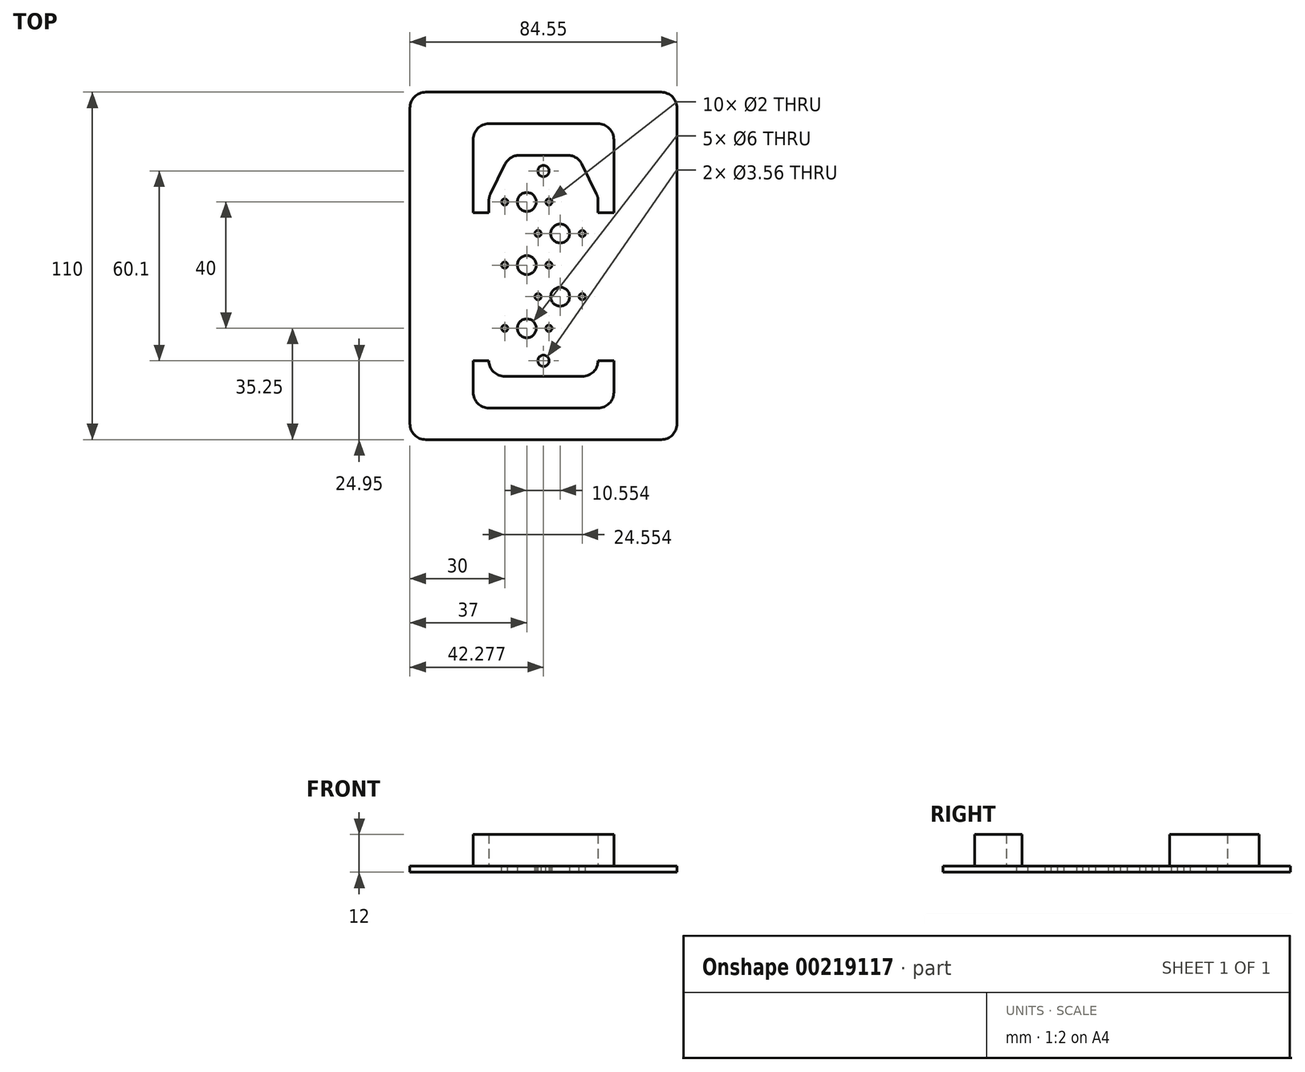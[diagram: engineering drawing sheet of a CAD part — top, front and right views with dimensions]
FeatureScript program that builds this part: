
annotation { "Feature Type Name" : "Feature", "Feature Type Description" : "" }
export const myFeature = defineFeature(function(context is Context, id is Id, definition is map)
    precondition{}
    {
        {
            var Q0;
            Q0=qCreatedBy(makeId("Top.planeOp"),FACE);
            var sketch = newSketch(context, id + "F0", { "sketchPlane" : qUnion([Q0])});
            skLineSegment(sketch, "E0", {"start": v(0, 0) * mm, "end": v(0, 5) * mm});
            skLineSegment(sketch, "E1", {"start": v(0, 56.78) * mm, "end": v(6.48, 70) * mm});
            skLineSegment(sketch, "E2", {"start": v(6.48, 70) * mm, "end": v(28.07, 70) * mm});
            skLineSegment(sketch, "E3", {"start": v(28.07, 70) * mm, "end": v(34.55, 56.78) * mm});
            skLineSegment(sketch, "E4", {"start": v(34.55, 56.78) * mm, "end": v(34.55, 51.78) * mm});
            skLineSegment(sketch, "E5", {"start": v(34.55, 0) * mm, "end": v(0, 0) * mm});
            skLineSegment(sketch, "E6", {"start": v(0, 51.78) * mm, "end": v(-5, 51.78) * mm});
            skLineSegment(sketch, "E7", {"start": v(-5, 51.78) * mm, "end": v(-5, 80) * mm});
            skLineSegment(sketch, "E8", {"start": v(-5, 80) * mm, "end": v(39.55, 80) * mm});
            skLineSegment(sketch, "E9", {"start": v(39.55, 80) * mm, "end": v(39.55, 51.78) * mm});
            skLineSegment(sketch, "E10", {"start": v(39.55, 51.78) * mm, "end": v(34.55, 51.78) * mm});
            skLineSegment(sketch, "E11", {"start": v(0, 5) * mm, "end": v(-5, 5) * mm});
            skLineSegment(sketch, "E12", {"start": v(-5, 5) * mm, "end": v(-5, -10) * mm});
            skLineSegment(sketch, "E13", {"start": v(-5, -10) * mm, "end": v(39.55, -10) * mm});
            skLineSegment(sketch, "E14", {"start": v(39.55, -10) * mm, "end": v(39.55, 5) * mm});
            skLineSegment(sketch, "E15", {"start": v(39.55, 5) * mm, "end": v(34.55, 5) * mm});
            skLineSegment(sketch, "E16", {"start": v(17.28, 70) * mm, "end": v(17.28, 0) * mm, "construction": true});
            skCircle(sketch, "E17", {"center": v(17.28, 65.05) * mm, "radius": 1.78 * mm});
            skCircle(sketch, "E18", {"center": v(17.28, 4.95) * mm, "radius": 1.78 * mm});
            skCircle(sketch, "E19", {"center": v(12, 35.25) * mm, "radius": 3 * mm});
            skCircle(sketch, "E20", {"center": v(22.55, 45.25) * mm, "radius": 3 * mm});
            skCircle(sketch, "E21", {"center": v(22.55, 25.25) * mm, "radius": 3 * mm});
            skCircle(sketch, "E22", {"center": v(12, 15.25) * mm, "radius": 3 * mm});
            skCircle(sketch, "E23", {"center": v(12, 55.25) * mm, "radius": 3 * mm});
            skPoint(sketch, "E24.startSnap0", {"position": v(17.28, 80) * mm});
            skPoint(sketch, "E25.endSnap0", {"position": v(0, 28.39) * mm});
            skLineSegment(sketch, "E26.bottom", {"start": v(-25, 90) * mm, "end": v(59.55, 90) * mm});
            skLineSegment(sketch, "E26.top", {"start": v(-25, -20) * mm, "end": v(59.55, -20) * mm});
            skLineSegment(sketch, "E26.left", {"start": v(-25, 90) * mm, "end": v(-25, -20) * mm});
            skLineSegment(sketch, "E26.right", {"start": v(59.55, 90) * mm, "end": v(59.55, -20) * mm});
            skLineSegment(sketch, "E27.trimOffspring", {"start": v(0, 51.78) * mm, "end": v(0, 56.78) * mm});
            skLineSegment(sketch, "E28.trimOffspring", {"start": v(34.55, 5) * mm, "end": v(34.55, 0) * mm});
            skSolve(sketch);
        }
        {
            var Q0;
            Q0=makeQuery(id+"F0.imprint","IMPRINT",FACE,{"disambiguationData":[TD([[makeQuery(id+"F0.imprint","IMPRINT",EDGE,{"derivedFrom":sQuery(id+"F0.wireOp",EDGE,"E0")}),-1.0]])]});
            extrude(context, id + "F1", {"entities" : qUnion([Q0]), "depth" : 2 * mm});
        }
        {
            var Q0;
            Q0=makeQuery(id+"F0.imprint","IMPRINT",FACE,{"disambiguationData":[TD([[makeQuery(id+"F0.imprint","IMPRINT",EDGE,{"derivedFrom":sQuery(id+"F0.wireOp",EDGE,"E1")}),1.0]])]});
            extrude(context, id + "F2", {"entities" : qUnion([Q0]), "operationType" : NewBodyOperationType.ADD, "depth" : 12 * mm});
        }
        {
            var Q0;
            Q0=makeQuery(id+"F0.imprint","IMPRINT",FACE,{"disambiguationData":[TD([[makeQuery(id+"F0.imprint","IMPRINT",EDGE,{"derivedFrom":sQuery(id+"F0.wireOp",EDGE,"E0")}),1.0]])]});
            extrude(context, id + "F3", {"entities" : qUnion([Q0]), "operationType" : NewBodyOperationType.ADD, "depth" : 12 * mm});
        }
        {
            var Q0;
            Q0=makeQuery(id+"F2.opExtrude","SWEPT_EDGE",EDGE,{"disambiguationData":[OSD([sQuery(id+"F0.wireOp",EDGE,"E1"),sQuery(id+"F0.wireOp",EDGE,"E2")])]});
            var Q1;
            Q1=makeQuery(id+"F2.opExtrude","SWEPT_EDGE",EDGE,{"disambiguationData":[OSD([sQuery(id+"F0.wireOp",EDGE,"E2"),sQuery(id+"F0.wireOp",EDGE,"E3")])]});
            var Q2;
            Q2=makeQuery(id+"F2.opExtrude","SWEPT_EDGE",EDGE,{"disambiguationData":[OSD([sQuery(id+"F0.wireOp",EDGE,"E1"),sQuery(id+"F0.wireOp",EDGE,"E27.trimOffspring")])]});
            var Q3;
            Q3=makeQuery(id+"F2.opExtrude","SWEPT_EDGE",EDGE,{"disambiguationData":[OSD([sQuery(id+"F0.wireOp",EDGE,"E3"),sQuery(id+"F0.wireOp",EDGE,"E4")])]});
            var Q4;
            Q4=makeQuery(id+"F3.opExtrude","SWEPT_EDGE",EDGE,{"disambiguationData":[OSD([sQuery(id+"F0.wireOp",EDGE,"E5"),sQuery(id+"F0.wireOp",EDGE,"E28.trimOffspring")])]});
            var Q5;
            Q5=makeQuery(id+"F3.opExtrude","SWEPT_EDGE",EDGE,{"disambiguationData":[OSD([sQuery(id+"F0.wireOp",EDGE,"E0"),sQuery(id+"F0.wireOp",EDGE,"E5")])]});
            var Q6;
            Q6=makeQuery(id+"F1.opExtrude","SWEPT_EDGE",EDGE,{"disambiguationData":[OSD([sQuery(id+"F0.wireOp",EDGE,"E26.top"),sQuery(id+"F0.wireOp",EDGE,"E26.right")])]});
            var Q7;
            Q7=makeQuery(id+"F1.opExtrude","SWEPT_EDGE",EDGE,{"disambiguationData":[OSD([sQuery(id+"F0.wireOp",EDGE,"E26.bottom"),sQuery(id+"F0.wireOp",EDGE,"E26.right")])]});
            var Q8;
            Q8=makeQuery(id+"F1.opExtrude","SWEPT_EDGE",EDGE,{"disambiguationData":[OSD([sQuery(id+"F0.wireOp",EDGE,"E26.bottom"),sQuery(id+"F0.wireOp",EDGE,"E26.left")])]});
            var Q9;
            Q9=makeQuery(id+"F1.opExtrude","SWEPT_EDGE",EDGE,{"disambiguationData":[OSD([sQuery(id+"F0.wireOp",EDGE,"E26.top"),sQuery(id+"F0.wireOp",EDGE,"E26.left")])]});
            fillet(context, id + "F4", {"entities" : qUnion([Q0, Q1, Q2, Q3, Q4, Q5, Q6, Q7, Q8, Q9]), "radius" : 5 * mm, "tangentPropagation" : true, "allowEdgeOverflow" : false});
        }
        {
            var Q0;
            Q0=makeQuery(id+"F3.opExtrude","SWEPT_EDGE",EDGE,{"disambiguationData":[OSD([sQuery(id+"F0.wireOp",EDGE,"E12"),sQuery(id+"F0.wireOp",EDGE,"E13")])]});
            var Q1;
            Q1=makeQuery(id+"F3.opExtrude","SWEPT_EDGE",EDGE,{"disambiguationData":[OSD([sQuery(id+"F0.wireOp",EDGE,"E13"),sQuery(id+"F0.wireOp",EDGE,"E14")])]});
            var Q2;
            Q2=makeQuery(id+"F2.opExtrude","SWEPT_EDGE",EDGE,{"disambiguationData":[OSD([sQuery(id+"F0.wireOp",EDGE,"E8"),sQuery(id+"F0.wireOp",EDGE,"E9")])]});
            var Q3;
            Q3=makeQuery(id+"F2.opExtrude","SWEPT_EDGE",EDGE,{"disambiguationData":[OSD([sQuery(id+"F0.wireOp",EDGE,"E7"),sQuery(id+"F0.wireOp",EDGE,"E8")])]});
            fillet(context, id + "F5", {"entities" : qUnion([Q0, Q1, Q2, Q3]), "radius" : 5 * mm, "tangentPropagation" : true, "allowEdgeOverflow" : false});
        }
        {
            var Q0;
            Q0=makeQuery(id+"F1.opExtrude","CAP_FACE",FACE,{"disambiguationData":[OSD([sQuery(id+"F0.wireOp",EDGE,"E0"),sQuery(id+"F0.wireOp",EDGE,"E1"),sQuery(id+"F0.wireOp",EDGE,"E2"),sQuery(id+"F0.wireOp",EDGE,"E3"),sQuery(id+"F0.wireOp",EDGE,"E4"),sQuery(id+"F0.wireOp",EDGE,"E5"),sQuery(id+"F0.wireOp",EDGE,"E6"),sQuery(id+"F0.wireOp",EDGE,"E7"),sQuery(id+"F0.wireOp",EDGE,"E8"),sQuery(id+"F0.wireOp",EDGE,"E9"),sQuery(id+"F0.wireOp",EDGE,"E10"),sQuery(id+"F0.wireOp",EDGE,"E11"),sQuery(id+"F0.wireOp",EDGE,"E12"),sQuery(id+"F0.wireOp",EDGE,"E13"),sQuery(id+"F0.wireOp",EDGE,"E14"),sQuery(id+"F0.wireOp",EDGE,"E15"),sQuery(id+"F0.wireOp",EDGE,"E17"),sQuery(id+"F0.wireOp",EDGE,"E18"),sQuery(id+"F0.wireOp",EDGE,"E19"),sQuery(id+"F0.wireOp",EDGE,"E20"),sQuery(id+"F0.wireOp",EDGE,"E21"),sQuery(id+"F0.wireOp",EDGE,"E22"),sQuery(id+"F0.wireOp",EDGE,"E23"),sQuery(id+"F0.wireOp",EDGE,"E26.bottom"),sQuery(id+"F0.wireOp",EDGE,"E26.top"),sQuery(id+"F0.wireOp",EDGE,"E26.left"),sQuery(id+"F0.wireOp",EDGE,"E26.right"),sQuery(id+"F0.wireOp",EDGE,"E27.trimOffspring"),sQuery(id+"F0.wireOp",EDGE,"E28.trimOffspring")])],"isStart":false});
            var sketch = newSketch(context, id + "F6", { "sketchPlane" : qUnion([Q0])});
            skCircle(sketch, "E29", {"center": v(5, 55.25) * mm, "radius": 1 * mm});
            skCircle(sketch, "E30", {"center": v(19, 55.25) * mm, "radius": 1 * mm});
            skCircle(sketch, "E31", {"center": v(19, 35.25) * mm, "radius": 1 * mm});
            skCircle(sketch, "E32", {"center": v(5, 35.25) * mm, "radius": 1 * mm});
            skCircle(sketch, "E33", {"center": v(15.55, 25.25) * mm, "radius": 1 * mm});
            skCircle(sketch, "E34", {"center": v(29.55, 25.25) * mm, "radius": 1 * mm});
            skCircle(sketch, "E35", {"center": v(15.55, 45.25) * mm, "radius": 1 * mm});
            skCircle(sketch, "E36", {"center": v(29.55, 45.25) * mm, "radius": 1 * mm});
            skCircle(sketch, "E37", {"center": v(5, 15.25) * mm, "radius": 1 * mm});
            skCircle(sketch, "E38", {"center": v(19, 15.25) * mm, "radius": 1 * mm});
            skSolve(sketch);
        }
        {
            var Q0;
            Q0=makeQuery(id+"F6.imprint","IMPRINT",FACE,{"disambiguationData":[TD([[makeQuery(id+"F6.imprint","IMPRINT",EDGE,{"derivedFrom":sQuery(id+"F6.wireOp",EDGE,"E29")}),1.0]])]});
            var Q1;
            Q1=makeQuery(id+"F6.imprint","IMPRINT",FACE,{"disambiguationData":[TD([[makeQuery(id+"F6.imprint","IMPRINT",EDGE,{"derivedFrom":sQuery(id+"F6.wireOp",EDGE,"E30")}),1.0]])]});
            var Q2;
            Q2=makeQuery(id+"F6.imprint","IMPRINT",FACE,{"disambiguationData":[TD([[makeQuery(id+"F6.imprint","IMPRINT",EDGE,{"derivedFrom":sQuery(id+"F6.wireOp",EDGE,"OHU8HePS-A5hE-2PZY-Okrr-ufKmC9e9iSHk")}),1.0]])]});
            var Q3;
            Q3=makeQuery(id+"F6.imprint","IMPRINT",FACE,{"disambiguationData":[TD([[makeQuery(id+"F6.imprint","IMPRINT",EDGE,{"derivedFrom":sQuery(id+"F6.wireOp",EDGE,"iaLojANe-PzYV-wCPD-OrHB-3U5ugpvtCpFz")}),1.0]])]});
            var Q4;
            Q4=makeQuery(id+"F6.imprint","IMPRINT",FACE,{"disambiguationData":[TD([[makeQuery(id+"F6.imprint","IMPRINT",EDGE,{"derivedFrom":sQuery(id+"F6.wireOp",EDGE,"E31")}),1.0]])]});
            var Q5;
            Q5=makeQuery(id+"F6.imprint","IMPRINT",FACE,{"disambiguationData":[TD([[makeQuery(id+"F6.imprint","IMPRINT",EDGE,{"derivedFrom":sQuery(id+"F6.wireOp",EDGE,"E32")}),1.0]])]});
            var Q6;
            Q6=makeQuery(id+"F6.imprint","IMPRINT",FACE,{"disambiguationData":[TD([[makeQuery(id+"F6.imprint","IMPRINT",EDGE,{"derivedFrom":sQuery(id+"F6.wireOp",EDGE,"HoPFKScR-o8aC-giok-rjnB-pm8gwUeQeGYI")}),1.0]])]});
            var Q7;
            Q7=makeQuery(id+"F6.imprint","IMPRINT",FACE,{"disambiguationData":[TD([[makeQuery(id+"F6.imprint","IMPRINT",EDGE,{"derivedFrom":sQuery(id+"F6.wireOp",EDGE,"E33")}),1.0]])]});
            var Q8;
            Q8=makeQuery(id+"F6.imprint","IMPRINT",FACE,{"disambiguationData":[TD([[makeQuery(id+"F6.imprint","IMPRINT",EDGE,{"derivedFrom":sQuery(id+"F6.wireOp",EDGE,"E34")}),1.0]])]});
            var Q9;
            Q9=makeQuery(id+"F6.imprint","IMPRINT",FACE,{"disambiguationData":[TD([[makeQuery(id+"F6.imprint","IMPRINT",EDGE,{"derivedFrom":sQuery(id+"F6.wireOp",EDGE,"kV2GfSh5-9EAK-eOVu-P3G4-iW580V03fMl9")}),1.0]])]});
            var Q10;
            Q10=sQuery(id+"F6.wireOp",EDGE,"E29");
            var Q11;
            Q11=sQuery(id+"F6.wireOp",EDGE,"E30");
            var Q12;
            Q12=sQuery(id+"F6.wireOp",EDGE,"iaLojANe-PzYV-wCPD-OrHB-3U5ugpvtCpFz");
            var Q13;
            Q13=sQuery(id+"F6.wireOp",EDGE,"E31");
            var Q14;
            Q14=sQuery(id+"F6.wireOp",EDGE,"OHU8HePS-A5hE-2PZY-Okrr-ufKmC9e9iSHk");
            var Q15;
            Q15=sQuery(id+"F6.wireOp",EDGE,"E32");
            var Q16;
            Q16=sQuery(id+"F6.wireOp",EDGE,"HoPFKScR-o8aC-giok-rjnB-pm8gwUeQeGYI");
            var Q17;
            Q17=sQuery(id+"F6.wireOp",EDGE,"E33");
            var Q18;
            Q18=sQuery(id+"F6.wireOp",EDGE,"kV2GfSh5-9EAK-eOVu-P3G4-iW580V03fMl9");
            var Q19;
            Q19=sQuery(id+"F6.wireOp",EDGE,"E34");
            extrude(context, id + "F7", {"entities" : qUnion([Q0, Q1, Q2, Q3, Q4, Q5, Q6, Q7, Q8, Q9]), "operationType" : NewBodyOperationType.REMOVE, "surfaceEntities" : qUnion([Q10, Q11, Q12, Q13, Q14, Q15, Q16, Q17, Q18, Q19]), "oppositeDirection" : true, "depth" : 25 * mm});
        }
        {
            var Q0;
            Q0 = qSketchRegion(id + "F6", true);
            extrude(context, id + "F8", {"entities" : qUnion([Q0]), "operationType" : NewBodyOperationType.REMOVE, "oppositeDirection" : true, "depth" : 25 * mm});
        }
    });
